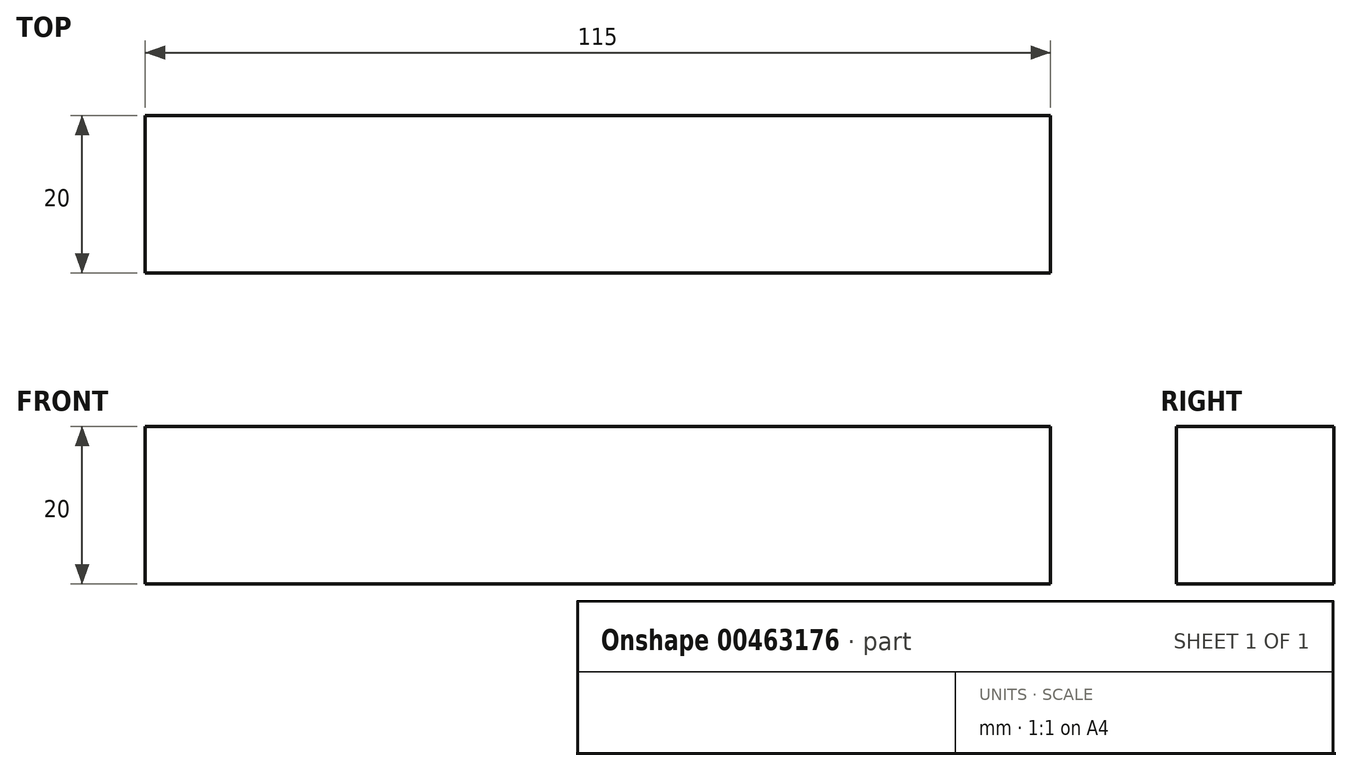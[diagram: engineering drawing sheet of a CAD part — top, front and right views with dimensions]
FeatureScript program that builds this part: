
annotation { "Feature Type Name" : "Feature", "Feature Type Description" : "" }
export const myFeature = defineFeature(function(context is Context, id is Id, definition is map)
    precondition{}
    {
        {
            var Q0;
            Q0=qCreatedBy(makeId("Front.planeOp"),FACE);
            var sketch = newSketch(context, id + "F0", { "sketchPlane" : qUnion([Q0])});
            skLineSegment(sketch, "E0.bottom", {"start": v(0, 0) * mm, "end": v(115, 0) * mm});
            skLineSegment(sketch, "E0.top", {"start": v(0, 20) * mm, "end": v(115, 20) * mm});
            skLineSegment(sketch, "E0.left", {"start": v(0, 0) * mm, "end": v(0, 20) * mm});
            skLineSegment(sketch, "E0.right", {"start": v(115, 0) * mm, "end": v(115, 20) * mm});
            skSolve(sketch);
        }
        {
            var Q0;
            Q0=makeQuery(id+"F0.imprint","IMPRINT",FACE,{"disambiguationData":[TD([[makeQuery(id+"F0.imprint","IMPRINT",EDGE,{"derivedFrom":sQuery(id+"F0.wireOp",EDGE,"E0.bottom")}),1.0]])]});
            extrude(context, id + "F1", {"entities" : qUnion([Q0]), "depth" : 20 * mm});
        }
    });
